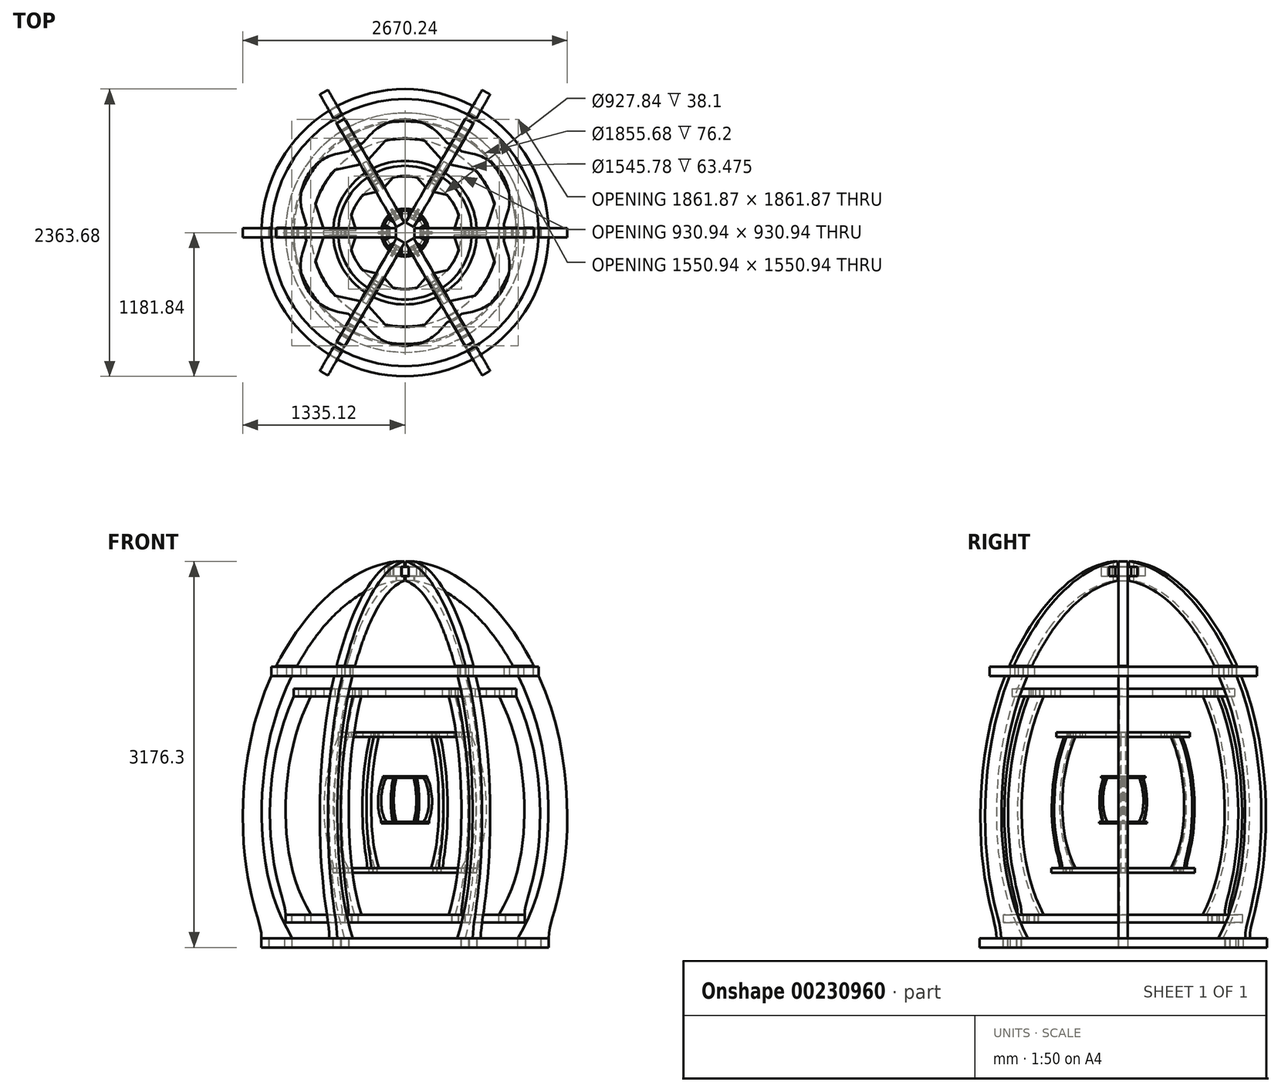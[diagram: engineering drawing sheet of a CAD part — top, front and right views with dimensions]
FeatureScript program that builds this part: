
annotation { "Feature Type Name" : "Feature", "Feature Type Description" : "" }
export const myFeature = defineFeature(function(context is Context, id is Id, definition is map)
    precondition{}
    {
        {
            var Q0;
            Q0=qCreatedBy(makeId("Front.planeOp"),FACE);
            var sketch = newSketch(context, id + "F0", { "sketchPlane" : qUnion([Q0])});
            skLineSegment(sketch, "E0", {"start": v(-1181.84, -1150.9) * mm, "end": v(-927.84, -1150.9) * mm});
            skFitSpline(sketch, "E1", {"points": [v(0, 1953.34) * mm, v(-1100.72, 1005.82) * mm, v(-1321.31, -446.03) * mm, v(-1216.83, -971.67) * mm, v(-1181.84, -1150.9) * mm], "startDerivative": vector(-4000.43, 5.06) * mm, "endDerivative": vector(0, -1489.55) * mm});
            skLineSegment(sketch, "E2", {"start": v(-1099.69, 1008.1) * mm, "end": v(-930.94, 1008.1) * mm});
            skLineSegment(sketch, "E3", {"start": v(-1181.84, -1150.9) * mm, "end": v(-1181.84, -1354.1) * mm});
            skLineSegment(sketch, "E4", {"start": v(-1181.84, -1354.1) * mm, "end": v(-877.04, -1354.1) * mm});
            skLineSegment(sketch, "E5", {"start": v(-877.04, -1354.1) * mm, "end": v(-877.04, -1252.5) * mm});
            skLineSegment(sketch, "E6", {"start": v(-877.04, -1252.5) * mm, "end": v(-927.84, -1252.5) * mm});
            skLineSegment(sketch, "E7", {"start": v(-927.84, -1252.5) * mm, "end": v(-927.84, -1150.9) * mm});
            skFitSpline(sketch, "E8.trimOffspring", {"points": [v(0, -1757.92) * mm, v(-927.84, -1150.9) * mm, v(-1179.31, -127.8) * mm, v(-917.89, 1034.08) * mm, v(0, 1800.66) * mm], "startDerivative": vector(-4973.2, 113.59) * mm, "endDerivative": vector(4756.7, 336.76) * mm});
            skLineSegment(sketch, "E9", {"start": v(-1023.33, 1160.5) * mm, "end": v(-848.12, 1160.5) * mm});
            skLineSegment(sketch, "E10", {"start": v(0, 1953.34) * mm, "end": v(0, 1800.66) * mm});
            skLineSegment(sketch, "E11.bottom", {"start": v(-1118.34, -1074.7) * mm, "end": v(-991.34, -1074.7) * mm});
            skLineSegment(sketch, "E11.top", {"start": v(-1118.34, -1227.1) * mm, "end": v(-991.34, -1227.1) * mm});
            skLineSegment(sketch, "E11.left", {"start": v(-1118.34, -1074.7) * mm, "end": v(-1118.34, -1227.1) * mm});
            skLineSegment(sketch, "E11.right", {"start": v(-991.34, -1074.7) * mm, "end": v(-991.34, -1227.1) * mm});
            skPoint(sketch, "E11.middle", {"position": v(-1054.84, -1150.9) * mm});
            skLineSegment(sketch, "E12.bottom", {"start": v(-1053.41, 1084.3) * mm, "end": v(-977.21, 1084.3) * mm});
            skLineSegment(sketch, "E12.top", {"start": v(-1053.41, 931.9) * mm, "end": v(-977.21, 931.9) * mm});
            skLineSegment(sketch, "E12.left", {"start": v(-1053.41, 1084.3) * mm, "end": v(-1053.41, 931.9) * mm});
            skLineSegment(sketch, "E12.right", {"start": v(-977.21, 1084.3) * mm, "end": v(-977.21, 931.9) * mm});
            skPoint(sketch, "E12.middle", {"position": v(-1015.31, 1008.1) * mm});
            skLineSegment(sketch, "E13", {"start": v(-891.46, 1084.3) * mm, "end": v(-1063.3, 1084.3) * mm});
            skLineSegment(sketch, "E14", {"start": v(-889.38, 1088.12) * mm, "end": v(-1061.37, 1088.12) * mm});
            skLineSegment(sketch, "E15", {"start": v(-76.2, 1949.19) * mm, "end": v(-76.2, 1791.3) * mm});
            skLineSegment(sketch, "E16", {"start": v(-76.2, 1791.3) * mm, "end": v(-76.2, 1829.15) * mm});
            skLineSegment(sketch, "E17", {"start": v(-76.2, 1829.15) * mm, "end": v(-127, 1829.15) * mm});
            skLineSegment(sketch, "E18", {"start": v(-127, 1829.15) * mm, "end": v(-127, 1905.35) * mm});
            skLineSegment(sketch, "E19", {"start": v(-127, 1905.35) * mm, "end": v(-76.2, 1905.35) * mm});
            skLineSegment(sketch, "E20", {"start": v(-889.38, 1088.12) * mm, "end": v(-811.35, 1088.12) * mm});
            skLineSegment(sketch, "E21", {"start": v(-811.35, 1088.12) * mm, "end": v(-680.59, 1399.42) * mm});
            skLineSegment(sketch, "E22", {"start": v(-811.35, 1088.12) * mm, "end": v(-811.35, 1013.84) * mm});
            skLineSegment(sketch, "E23", {"start": v(-811.35, 1013.84) * mm, "end": v(-933.78, 1013.84) * mm});
            skLineSegment(sketch, "E24", {"start": v(-933.78, 1013.84) * mm, "end": v(-933.78, 1088.12) * mm});
            skSolve(sketch);
        }
        {
            var Q0;
            {var subQ5=sQuery(id+"F0.wireOp",EDGE,"E12.bottom");Q0=makeQuery(id+"F0.imprint","IMPRINT",FACE,{"disambiguationData":[TD([[makeQuery(id+"F0.imprint","IMPRINT",EDGE,{"derivedFrom":subQ5}),-1.0]])]});}
            var Q1;
            {var subQ5=sQuery(id+"F0.wireOp",EDGE,"E11.top");Q1=makeQuery(id+"F0.imprint","IMPRINT",FACE,{"disambiguationData":[TD([[makeQuery(id+"F0.imprint","IMPRINT",EDGE,{"derivedFrom":subQ5}),1.0]])]});}
            var Q2;
            {var subQ0=sQuery(id+"F0.wireOp",EDGE,"E11.left");var subQ3=sQuery(id+"F0.wireOp",EDGE,"E0");var subQ4=makeQuery(id+"F0.imprint","INTERSECT",VERTEX,{"derivedFrom":[subQ3,subQ0]});Q2=makeQuery(id+"F0.imprint","IMPRINT",FACE,{"disambiguationData":[TD([[makeQuery(id+"F0.imprint","IMPRINT",EDGE,{"disambiguationData":[TD([[subQ4,-1.0]])],"derivedFrom":subQ3}),1.0]])]});}
            var Q3;
            {var subQ0=sQuery(id+"F0.wireOp",EDGE,"E2");var subQ1=sQuery(id+"F0.wireOp",EDGE,"E1");var subQ2=makeQuery(id+"F0.imprint","INTERSECT",VERTEX,{"derivedFrom":[subQ1,subQ0]});Q3=makeQuery(id+"F0.imprint","IMPRINT",FACE,{"disambiguationData":[TD([[makeQuery(id+"F0.imprint","IMPRINT",EDGE,{"disambiguationData":[TD([[subQ2,-1.0]])],"derivedFrom":subQ0}),-1.0]])]});}
            var Q4;
            {var subQ0=sQuery(id+"F0.wireOp",EDGE,"E8.trimOffspring");var subQ1=sQuery(id+"F0.wireOp",EDGE,"E2");var subQ2=makeQuery(id+"F0.imprint","INTERSECT",VERTEX,{"derivedFrom":[subQ1,subQ0]});Q4=makeQuery(id+"F0.imprint","IMPRINT",FACE,{"disambiguationData":[TD([[makeQuery(id+"F0.imprint","IMPRINT",EDGE,{"disambiguationData":[TD([[subQ2,1.0]])],"derivedFrom":subQ1}),-1.0]])]});}
            var Q5;
            {var subQ0=sQuery(id+"F0.wireOp",EDGE,"E12.left");var subQ5=sQuery(id+"F0.wireOp",EDGE,"E2");var subQ6=makeQuery(id+"F0.imprint","INTERSECT",VERTEX,{"derivedFrom":[subQ5,subQ0]});Q5=makeQuery(id+"F0.imprint","IMPRINT",FACE,{"disambiguationData":[TD([[makeQuery(id+"F0.imprint","IMPRINT",EDGE,{"disambiguationData":[TD([[subQ6,-1.0]])],"derivedFrom":subQ5}),-1.0]])]});}
            var Q6;
            {var subQ0=sQuery(id+"F0.wireOp",EDGE,"E12.left");var subQ1=sQuery(id+"F0.wireOp",EDGE,"E2");var subQ2=makeQuery(id+"F0.imprint","INTERSECT",VERTEX,{"derivedFrom":[subQ1,subQ0]});Q6=makeQuery(id+"F0.imprint","IMPRINT",FACE,{"disambiguationData":[TD([[makeQuery(id+"F0.imprint","IMPRINT",EDGE,{"disambiguationData":[TD([[subQ2,-1.0]])],"derivedFrom":subQ1}),1.0]])]});}
            extrude(context, id + "F1", {"entities" : qUnion([Q0, Q1, Q2, Q3, Q4, Q5, Q6]), "endBound" : BoundingType.SYMMETRIC, "depth" : 76.2 * mm});
        }
        {
            var Q0;
            Q0=makeQuery(id+"F1.opExtrude","SWEPT_BODY",BODY,{"disambiguationData":[OSD([sQuery(id+"F0.wireOp",EDGE,"E0"),sQuery(id+"F0.wireOp",EDGE,"E1"),sQuery(id+"F0.wireOp",EDGE,"E2"),sQuery(id+"F0.wireOp",EDGE,"E8.trimOffspring")])]});
            var Q1;
            Q1=sQuery(id+"F0.wireOp",EDGE,"E10");
            circularPattern(context, id + "F2", {"entities" : qUnion([Q0]), "axis" : qUnion([Q1]), "angle" : 360 * degree, "instanceCount" : 6, "equalSpace" : true});
        }
        {
            var Q0;
            Q0=qCreatedBy(makeId("Top.planeOp"),FACE);
            var Q1;
            Q1=sQuery(id+"F0.wireOp",VERTEX,"E8.trimOffspring.1.internal");
            cPlane(context, id + "F3", {"entities" : qUnion([Q0, Q1]), "cplaneType" : CPlaneType.PLANE_POINT, "offset" : 25.4 * mm, "width" : 152.4 * mm, "height" : 152.4 * mm});
        }
        {
            var Q0;
            Q0=qCreatedBy(id+"F3.planeOp",FACE);
            var sketch = newSketch(context, id + "F4", { "sketchPlane" : qUnion([Q0])});
            skCircle(sketch, "E25", {"center": v(0, 0) * mm, "radius": 1181.84 * mm});
            skCircle(sketch, "E26", {"center": v(0, 0) * mm, "radius": 927.84 * mm});
            skLineSegment(sketch, "E27.bottom", {"start": v(-1118.98, 38.73) * mm, "end": v(-990.7, 38.73) * mm});
            skLineSegment(sketch, "E27.top", {"start": v(-1118.98, -38.74) * mm, "end": v(-990.7, -38.74) * mm});
            skLineSegment(sketch, "E27.left", {"start": v(-1118.98, 38.73) * mm, "end": v(-1118.98, -38.74) * mm});
            skLineSegment(sketch, "E27.right", {"start": v(-990.7, 38.73) * mm, "end": v(-990.7, -38.74) * mm});
            skPoint(sketch, "E27.middle", {"position": v(-1054.84, 0) * mm});
            skLineSegment(sketch, "E28.1.0", {"start": v(-593.03, -949.7) * mm, "end": v(-528.9, -838.6) * mm});
            skLineSegment(sketch, "E28.1.1", {"start": v(-593.03, -949.7) * mm, "end": v(-525.94, -988.43) * mm});
            skLineSegment(sketch, "E28.1.2", {"start": v(-525.94, -988.43) * mm, "end": v(-461.8, -877.34) * mm});
            skLineSegment(sketch, "E28.1.3", {"start": v(-528.9, -838.6) * mm, "end": v(-461.8, -877.34) * mm});
            skLineSegment(sketch, "E28.2.0", {"start": v(525.94, -988.43) * mm, "end": v(461.8, -877.34) * mm});
            skLineSegment(sketch, "E28.2.1", {"start": v(525.94, -988.43) * mm, "end": v(593.03, -949.7) * mm});
            skLineSegment(sketch, "E28.2.2", {"start": v(593.03, -949.7) * mm, "end": v(528.9, -838.6) * mm});
            skLineSegment(sketch, "E28.2.3", {"start": v(461.8, -877.34) * mm, "end": v(528.9, -838.6) * mm});
            skLineSegment(sketch, "E28.3.0", {"start": v(1118.98, -38.74) * mm, "end": v(990.7, -38.74) * mm});
            skLineSegment(sketch, "E28.3.1", {"start": v(1118.98, -38.74) * mm, "end": v(1118.98, 38.73) * mm});
            skLineSegment(sketch, "E28.3.2", {"start": v(1118.98, 38.73) * mm, "end": v(990.7, 38.73) * mm});
            skLineSegment(sketch, "E28.3.3", {"start": v(990.7, -38.74) * mm, "end": v(990.7, 38.73) * mm});
            skLineSegment(sketch, "E28.4.0", {"start": v(593.03, 949.7) * mm, "end": v(528.9, 838.6) * mm});
            skLineSegment(sketch, "E28.4.1", {"start": v(593.03, 949.7) * mm, "end": v(525.94, 988.43) * mm});
            skLineSegment(sketch, "E28.4.2", {"start": v(525.94, 988.43) * mm, "end": v(461.8, 877.34) * mm});
            skLineSegment(sketch, "E28.4.3", {"start": v(528.9, 838.6) * mm, "end": v(461.8, 877.34) * mm});
            skLineSegment(sketch, "E28.5.0", {"start": v(-525.94, 988.43) * mm, "end": v(-461.8, 877.34) * mm});
            skLineSegment(sketch, "E28.5.1", {"start": v(-525.94, 988.43) * mm, "end": v(-593.03, 949.7) * mm});
            skLineSegment(sketch, "E28.5.2", {"start": v(-593.03, 949.7) * mm, "end": v(-528.9, 838.6) * mm});
            skLineSegment(sketch, "E28.5.3", {"start": v(-461.8, 877.34) * mm, "end": v(-528.9, 838.6) * mm});
            skSolve(sketch);
        }
        {
            var Q0;
            Q0=makeQuery(id+"F4.imprint","IMPRINT",FACE,{"disambiguationData":[TD([[makeQuery(id+"F4.imprint","IMPRINT",EDGE,{"derivedFrom":sQuery(id+"F4.wireOp",EDGE,"E25")}),1.0]])]});
            extrude(context, id + "F5", {"entities" : qUnion([Q0]), "oppositeDirection" : true, "depth" : 76.2 * mm});
        }
        {
            var Q0;
            Q0=qCreatedBy(makeId("Top.planeOp"),FACE);
            var Q1;
            Q1=sQuery(id+"F0.wireOp",VERTEX,"E2.end");
            cPlane(context, id + "F6", {"entities" : qUnion([Q0, Q1]), "cplaneType" : CPlaneType.PLANE_POINT, "offset" : 25.4 * mm, "width" : 152.4 * mm, "height" : 152.4 * mm});
        }
        {
            var Q0;
            Q0=qCreatedBy(id+"F6.planeOp",FACE);
            var sketch = newSketch(context, id + "F7", { "sketchPlane" : qUnion([Q0])});
            skCircle(sketch, "E29", {"center": v(0, 0) * mm, "radius": 1099.69 * mm});
            skCircle(sketch, "E30", {"center": v(0, 0) * mm, "radius": 930.94 * mm});
            skLineSegment(sketch, "E31.bottom", {"start": v(-1054.05, 38.74) * mm, "end": v(-976.58, 38.74) * mm});
            skLineSegment(sketch, "E31.top", {"start": v(-1054.05, -38.73) * mm, "end": v(-976.58, -38.73) * mm});
            skLineSegment(sketch, "E31.left", {"start": v(-1054.05, 38.74) * mm, "end": v(-1054.05, -38.73) * mm});
            skLineSegment(sketch, "E31.right", {"start": v(-976.58, 38.74) * mm, "end": v(-976.58, -38.73) * mm});
            skPoint(sketch, "E31.middle", {"position": v(-1015.31, 0) * mm});
            skLineSegment(sketch, "E32.1.0", {"start": v(-560.57, -893.46) * mm, "end": v(-521.83, -826.37) * mm});
            skLineSegment(sketch, "E32.1.1", {"start": v(-560.57, -893.46) * mm, "end": v(-493.48, -932.2) * mm});
            skLineSegment(sketch, "E32.1.2", {"start": v(-493.48, -932.2) * mm, "end": v(-454.74, -865.1) * mm});
            skLineSegment(sketch, "E32.1.3", {"start": v(-521.83, -826.37) * mm, "end": v(-454.74, -865.1) * mm});
            skLineSegment(sketch, "E32.2.0", {"start": v(493.48, -932.2) * mm, "end": v(454.74, -865.1) * mm});
            skLineSegment(sketch, "E32.2.1", {"start": v(493.48, -932.2) * mm, "end": v(560.57, -893.46) * mm});
            skLineSegment(sketch, "E32.2.2", {"start": v(560.57, -893.46) * mm, "end": v(521.83, -826.37) * mm});
            skLineSegment(sketch, "E32.2.3", {"start": v(454.74, -865.1) * mm, "end": v(521.83, -826.37) * mm});
            skLineSegment(sketch, "E32.3.0", {"start": v(1054.05, -38.74) * mm, "end": v(976.58, -38.74) * mm});
            skLineSegment(sketch, "E32.3.1", {"start": v(1054.05, -38.74) * mm, "end": v(1054.05, 38.73) * mm});
            skLineSegment(sketch, "E32.3.2", {"start": v(1054.05, 38.73) * mm, "end": v(976.58, 38.73) * mm});
            skLineSegment(sketch, "E32.3.3", {"start": v(976.58, -38.74) * mm, "end": v(976.58, 38.73) * mm});
            skLineSegment(sketch, "E32.4.0", {"start": v(560.57, 893.46) * mm, "end": v(521.83, 826.37) * mm});
            skLineSegment(sketch, "E32.4.1", {"start": v(560.57, 893.46) * mm, "end": v(493.48, 932.2) * mm});
            skLineSegment(sketch, "E32.4.2", {"start": v(493.48, 932.2) * mm, "end": v(454.74, 865.1) * mm});
            skLineSegment(sketch, "E32.4.3", {"start": v(521.83, 826.37) * mm, "end": v(454.74, 865.1) * mm});
            skLineSegment(sketch, "E32.5.0", {"start": v(-493.48, 932.2) * mm, "end": v(-454.74, 865.1) * mm});
            skLineSegment(sketch, "E32.5.1", {"start": v(-493.48, 932.2) * mm, "end": v(-560.57, 893.46) * mm});
            skLineSegment(sketch, "E32.5.2", {"start": v(-560.57, 893.46) * mm, "end": v(-521.83, 826.37) * mm});
            skLineSegment(sketch, "E32.5.3", {"start": v(-454.74, 865.1) * mm, "end": v(-521.83, 826.37) * mm});
            skLineSegment(sketch, "E33", {"start": v(-930.13, 38.73) * mm, "end": v(-803.13, 38.73) * mm});
            skLineSegment(sketch, "E34", {"start": v(-930.13, -38.74) * mm, "end": v(-803.13, -38.73) * mm});
            skLineSegment(sketch, "E35", {"start": v(-803.13, 38.74) * mm, "end": v(-803.13, -38.74) * mm, "construction": true});
            skLineSegment(sketch, "E36", {"start": v(-803.13, 0) * mm, "end": v(0, 0) * mm, "construction": true});
            skLineSegment(sketch, "E37", {"start": v(-803.13, 38.73) * mm, "end": v(-884.69, 289.77) * mm});
            skLineSegment(sketch, "E38", {"start": v(-803.13, -38.73) * mm, "end": v(-884.69, -289.77) * mm});
            skLineSegment(sketch, "E39.1.0", {"start": v(-435.11, -676.16) * mm, "end": v(-693.3, -621.28) * mm});
            skLineSegment(sketch, "E39.1.1", {"start": v(-498.61, -786.15) * mm, "end": v(-435.11, -676.16) * mm});
            skLineSegment(sketch, "E39.1.2", {"start": v(-431.52, -824.88) * mm, "end": v(-368.02, -714.9) * mm});
            skLineSegment(sketch, "E39.1.3", {"start": v(-368.02, -714.9) * mm, "end": v(-191.4, -911.05) * mm});
            skLineSegment(sketch, "E39.2.0", {"start": v(368.02, -714.9) * mm, "end": v(191.4, -911.05) * mm});
            skLineSegment(sketch, "E39.2.1", {"start": v(431.52, -824.88) * mm, "end": v(368.02, -714.9) * mm});
            skLineSegment(sketch, "E39.2.2", {"start": v(498.61, -786.15) * mm, "end": v(435.11, -676.16) * mm});
            skLineSegment(sketch, "E39.2.3", {"start": v(435.11, -676.16) * mm, "end": v(693.3, -621.28) * mm});
            skLineSegment(sketch, "E39.3.0", {"start": v(803.13, -38.74) * mm, "end": v(884.69, -289.77) * mm});
            skLineSegment(sketch, "E39.3.1", {"start": v(930.13, -38.74) * mm, "end": v(803.13, -38.74) * mm});
            skLineSegment(sketch, "E39.3.2", {"start": v(930.13, 38.73) * mm, "end": v(803.13, 38.73) * mm});
            skLineSegment(sketch, "E39.3.3", {"start": v(803.13, 38.73) * mm, "end": v(884.69, 289.77) * mm});
            skLineSegment(sketch, "E39.4.0", {"start": v(435.11, 676.16) * mm, "end": v(693.3, 621.28) * mm});
            skLineSegment(sketch, "E39.4.1", {"start": v(498.61, 786.15) * mm, "end": v(435.11, 676.16) * mm});
            skLineSegment(sketch, "E39.4.2", {"start": v(431.52, 824.88) * mm, "end": v(368.02, 714.9) * mm});
            skLineSegment(sketch, "E39.4.3", {"start": v(368.02, 714.9) * mm, "end": v(191.4, 911.05) * mm});
            skLineSegment(sketch, "E39.5.0", {"start": v(-368.02, 714.9) * mm, "end": v(-191.4, 911.05) * mm});
            skLineSegment(sketch, "E39.5.1", {"start": v(-431.52, 824.88) * mm, "end": v(-368.02, 714.9) * mm});
            skLineSegment(sketch, "E39.5.2", {"start": v(-498.61, 786.15) * mm, "end": v(-435.11, 676.16) * mm});
            skLineSegment(sketch, "E39.5.3", {"start": v(-435.11, 676.16) * mm, "end": v(-693.3, 621.28) * mm});
            skSolve(sketch);
        }
        {
            var Q0;
            Q0=makeQuery(id+"F7.imprint","IMPRINT",FACE,{"disambiguationData":[TD([[makeQuery(id+"F7.imprint","IMPRINT",EDGE,{"derivedFrom":sQuery(id+"F7.wireOp",EDGE,"E29")}),1.0]])]});
            var Q1;
            {var subQ0=sQuery(id+"F7.wireOp",EDGE,"E34");Q1=makeQuery(id+"F7.imprint","IMPRINT",FACE,{"disambiguationData":[TD([[makeQuery(id+"F7.imprint","IMPRINT",EDGE,{"derivedFrom":subQ0}),-1.0]])]});}
            var Q2;
            {var subQ0=sQuery(id+"F7.wireOp",EDGE,"E33");Q2=makeQuery(id+"F7.imprint","IMPRINT",FACE,{"disambiguationData":[TD([[makeQuery(id+"F7.imprint","IMPRINT",EDGE,{"derivedFrom":subQ0}),1.0]])]});}
            var Q3;
            {var subQ0=sQuery(id+"F7.wireOp",EDGE,"E39.5.2");Q3=makeQuery(id+"F7.imprint","IMPRINT",FACE,{"disambiguationData":[TD([[makeQuery(id+"F7.imprint","IMPRINT",EDGE,{"derivedFrom":subQ0}),-1.0]])]});}
            var Q4;
            {var subQ0=sQuery(id+"F7.wireOp",EDGE,"E39.5.0");Q4=makeQuery(id+"F7.imprint","IMPRINT",FACE,{"disambiguationData":[TD([[makeQuery(id+"F7.imprint","IMPRINT",EDGE,{"derivedFrom":subQ0}),1.0]])]});}
            var Q5;
            {var subQ0=sQuery(id+"F7.wireOp",EDGE,"E39.4.2");Q5=makeQuery(id+"F7.imprint","IMPRINT",FACE,{"disambiguationData":[TD([[makeQuery(id+"F7.imprint","IMPRINT",EDGE,{"derivedFrom":subQ0}),-1.0]])]});}
            var Q6;
            {var subQ0=sQuery(id+"F7.wireOp",EDGE,"E39.4.0");Q6=makeQuery(id+"F7.imprint","IMPRINT",FACE,{"disambiguationData":[TD([[makeQuery(id+"F7.imprint","IMPRINT",EDGE,{"derivedFrom":subQ0}),1.0]])]});}
            var Q7;
            {var subQ0=sQuery(id+"F7.wireOp",EDGE,"E39.3.2");Q7=makeQuery(id+"F7.imprint","IMPRINT",FACE,{"disambiguationData":[TD([[makeQuery(id+"F7.imprint","IMPRINT",EDGE,{"derivedFrom":subQ0}),-1.0]])]});}
            var Q8;
            {var subQ0=sQuery(id+"F7.wireOp",EDGE,"E39.3.0");Q8=makeQuery(id+"F7.imprint","IMPRINT",FACE,{"disambiguationData":[TD([[makeQuery(id+"F7.imprint","IMPRINT",EDGE,{"derivedFrom":subQ0}),1.0]])]});}
            var Q9;
            {var subQ0=sQuery(id+"F7.wireOp",EDGE,"E39.2.2");Q9=makeQuery(id+"F7.imprint","IMPRINT",FACE,{"disambiguationData":[TD([[makeQuery(id+"F7.imprint","IMPRINT",EDGE,{"derivedFrom":subQ0}),-1.0]])]});}
            var Q10;
            {var subQ0=sQuery(id+"F7.wireOp",EDGE,"E39.2.0");Q10=makeQuery(id+"F7.imprint","IMPRINT",FACE,{"disambiguationData":[TD([[makeQuery(id+"F7.imprint","IMPRINT",EDGE,{"derivedFrom":subQ0}),1.0]])]});}
            var Q11;
            {var subQ0=sQuery(id+"F7.wireOp",EDGE,"E39.1.2");Q11=makeQuery(id+"F7.imprint","IMPRINT",FACE,{"disambiguationData":[TD([[makeQuery(id+"F7.imprint","IMPRINT",EDGE,{"derivedFrom":subQ0}),-1.0]])]});}
            var Q12;
            {var subQ0=sQuery(id+"F7.wireOp",EDGE,"E39.1.0");Q12=makeQuery(id+"F7.imprint","IMPRINT",FACE,{"disambiguationData":[TD([[makeQuery(id+"F7.imprint","IMPRINT",EDGE,{"derivedFrom":subQ0}),1.0]])]});}
            extrude(context, id + "F8", {"entities" : qUnion([Q0, Q1, Q2, Q3, Q4, Q5, Q6, Q7, Q8, Q9, Q10, Q11, Q12]), "depth" : 76.2 * mm});
        }
        {
            var Q0;
            Q0=makeQuery(id+"F8.opExtrude","SWEPT_BODY",BODY,{"disambiguationData":[OSD([sQuery(id+"F7.wireOp",EDGE,"E29"),sQuery(id+"F7.wireOp",EDGE,"E30"),sQuery(id+"F7.wireOp",EDGE,"E31.bottom"),sQuery(id+"F7.wireOp",EDGE,"E31.top"),sQuery(id+"F7.wireOp",EDGE,"E31.left"),sQuery(id+"F7.wireOp",EDGE,"E31.right"),sQuery(id+"F7.wireOp",EDGE,"E32.1.0"),sQuery(id+"F7.wireOp",EDGE,"E32.1.1"),sQuery(id+"F7.wireOp",EDGE,"E32.1.2"),sQuery(id+"F7.wireOp",EDGE,"E32.1.3"),sQuery(id+"F7.wireOp",EDGE,"E32.2.0"),sQuery(id+"F7.wireOp",EDGE,"E32.2.1"),sQuery(id+"F7.wireOp",EDGE,"E32.2.2"),sQuery(id+"F7.wireOp",EDGE,"E32.2.3"),sQuery(id+"F7.wireOp",EDGE,"E32.3.0"),sQuery(id+"F7.wireOp",EDGE,"E32.3.1"),sQuery(id+"F7.wireOp",EDGE,"E32.3.2"),sQuery(id+"F7.wireOp",EDGE,"E32.3.3"),sQuery(id+"F7.wireOp",EDGE,"E32.4.0"),sQuery(id+"F7.wireOp",EDGE,"E32.4.1"),sQuery(id+"F7.wireOp",EDGE,"E32.4.2"),sQuery(id+"F7.wireOp",EDGE,"E32.4.3"),sQuery(id+"F7.wireOp",EDGE,"E32.5.0"),sQuery(id+"F7.wireOp",EDGE,"E32.5.1"),sQuery(id+"F7.wireOp",EDGE,"E32.5.2"),sQuery(id+"F7.wireOp",EDGE,"E32.5.3")])]});
            var Q1;
            Q1=makeQuery(id+"F1.opExtrude","SWEPT_BODY",BODY,{"disambiguationData":[OSD([sQuery(id+"F0.wireOp",EDGE,"E0"),sQuery(id+"F0.wireOp",EDGE,"E1"),sQuery(id+"F0.wireOp",EDGE,"E2"),sQuery(id+"F0.wireOp",EDGE,"E8.trimOffspring"),sQuery(id+"F0.wireOp",EDGE,"E11.top"),sQuery(id+"F0.wireOp",EDGE,"E11.left"),sQuery(id+"F0.wireOp",EDGE,"E11.right"),sQuery(id+"F0.wireOp",EDGE,"E12.bottom"),sQuery(id+"F0.wireOp",EDGE,"E12.left"),sQuery(id+"F0.wireOp",EDGE,"E12.right")])]});
            var Q2;
            Q2=makeQuery(id+"F2.opPattern","COPY",BODY,{"derivedFrom":makeQuery(id+"F1.opExtrude","SWEPT_BODY",BODY,{"disambiguationData":[OSD([sQuery(id+"F0.wireOp",EDGE,"E0"),sQuery(id+"F0.wireOp",EDGE,"E1"),sQuery(id+"F0.wireOp",EDGE,"E2"),sQuery(id+"F0.wireOp",EDGE,"E8.trimOffspring"),sQuery(id+"F0.wireOp",EDGE,"E11.top"),sQuery(id+"F0.wireOp",EDGE,"E11.left"),sQuery(id+"F0.wireOp",EDGE,"E11.right"),sQuery(id+"F0.wireOp",EDGE,"E12.bottom"),sQuery(id+"F0.wireOp",EDGE,"E12.left"),sQuery(id+"F0.wireOp",EDGE,"E12.right")])]}),"instanceName":"5"});
            var Q3;
            Q3=makeQuery(id+"F2.opPattern","COPY",BODY,{"derivedFrom":makeQuery(id+"F1.opExtrude","SWEPT_BODY",BODY,{"disambiguationData":[OSD([sQuery(id+"F0.wireOp",EDGE,"E0"),sQuery(id+"F0.wireOp",EDGE,"E1"),sQuery(id+"F0.wireOp",EDGE,"E2"),sQuery(id+"F0.wireOp",EDGE,"E8.trimOffspring"),sQuery(id+"F0.wireOp",EDGE,"E11.top"),sQuery(id+"F0.wireOp",EDGE,"E11.left"),sQuery(id+"F0.wireOp",EDGE,"E11.right"),sQuery(id+"F0.wireOp",EDGE,"E12.bottom"),sQuery(id+"F0.wireOp",EDGE,"E12.left"),sQuery(id+"F0.wireOp",EDGE,"E12.right")])]}),"instanceName":"1"});
            var Q4;
            Q4=makeQuery(id+"F2.opPattern","COPY",BODY,{"derivedFrom":makeQuery(id+"F1.opExtrude","SWEPT_BODY",BODY,{"disambiguationData":[OSD([sQuery(id+"F0.wireOp",EDGE,"E0"),sQuery(id+"F0.wireOp",EDGE,"E1"),sQuery(id+"F0.wireOp",EDGE,"E2"),sQuery(id+"F0.wireOp",EDGE,"E8.trimOffspring"),sQuery(id+"F0.wireOp",EDGE,"E11.top"),sQuery(id+"F0.wireOp",EDGE,"E11.left"),sQuery(id+"F0.wireOp",EDGE,"E11.right"),sQuery(id+"F0.wireOp",EDGE,"E12.bottom"),sQuery(id+"F0.wireOp",EDGE,"E12.left"),sQuery(id+"F0.wireOp",EDGE,"E12.right")])]}),"instanceName":"2"});
            var Q5;
            Q5=makeQuery(id+"F2.opPattern","COPY",BODY,{"derivedFrom":makeQuery(id+"F1.opExtrude","SWEPT_BODY",BODY,{"disambiguationData":[OSD([sQuery(id+"F0.wireOp",EDGE,"E0"),sQuery(id+"F0.wireOp",EDGE,"E1"),sQuery(id+"F0.wireOp",EDGE,"E2"),sQuery(id+"F0.wireOp",EDGE,"E8.trimOffspring"),sQuery(id+"F0.wireOp",EDGE,"E11.top"),sQuery(id+"F0.wireOp",EDGE,"E11.left"),sQuery(id+"F0.wireOp",EDGE,"E11.right"),sQuery(id+"F0.wireOp",EDGE,"E12.bottom"),sQuery(id+"F0.wireOp",EDGE,"E12.left"),sQuery(id+"F0.wireOp",EDGE,"E12.right")])]}),"instanceName":"3"});
            var Q6;
            Q6=makeQuery(id+"F2.opPattern","COPY",BODY,{"derivedFrom":makeQuery(id+"F1.opExtrude","SWEPT_BODY",BODY,{"disambiguationData":[OSD([sQuery(id+"F0.wireOp",EDGE,"E0"),sQuery(id+"F0.wireOp",EDGE,"E1"),sQuery(id+"F0.wireOp",EDGE,"E2"),sQuery(id+"F0.wireOp",EDGE,"E8.trimOffspring"),sQuery(id+"F0.wireOp",EDGE,"E11.top"),sQuery(id+"F0.wireOp",EDGE,"E11.left"),sQuery(id+"F0.wireOp",EDGE,"E11.right"),sQuery(id+"F0.wireOp",EDGE,"E12.bottom"),sQuery(id+"F0.wireOp",EDGE,"E12.left"),sQuery(id+"F0.wireOp",EDGE,"E12.right")])]}),"instanceName":"4"});
            var Q7;
            Q7=makeQuery(id+"F5.opExtrude","SWEPT_BODY",BODY,{"disambiguationData":[OSD([sQuery(id+"F4.wireOp",EDGE,"E25"),sQuery(id+"F4.wireOp",EDGE,"E26"),sQuery(id+"F4.wireOp",EDGE,"E27.bottom"),sQuery(id+"F4.wireOp",EDGE,"E27.top"),sQuery(id+"F4.wireOp",EDGE,"E27.left"),sQuery(id+"F4.wireOp",EDGE,"E27.right"),sQuery(id+"F4.wireOp",EDGE,"E28.1.0"),sQuery(id+"F4.wireOp",EDGE,"E28.1.1"),sQuery(id+"F4.wireOp",EDGE,"E28.1.2"),sQuery(id+"F4.wireOp",EDGE,"E28.1.3"),sQuery(id+"F4.wireOp",EDGE,"E28.2.0"),sQuery(id+"F4.wireOp",EDGE,"E28.2.1"),sQuery(id+"F4.wireOp",EDGE,"E28.2.2"),sQuery(id+"F4.wireOp",EDGE,"E28.2.3"),sQuery(id+"F4.wireOp",EDGE,"E28.3.0"),sQuery(id+"F4.wireOp",EDGE,"E28.3.1"),sQuery(id+"F4.wireOp",EDGE,"E28.3.2"),sQuery(id+"F4.wireOp",EDGE,"E28.3.3"),sQuery(id+"F4.wireOp",EDGE,"E28.4.0"),sQuery(id+"F4.wireOp",EDGE,"E28.4.1"),sQuery(id+"F4.wireOp",EDGE,"E28.4.2"),sQuery(id+"F4.wireOp",EDGE,"E28.4.3"),sQuery(id+"F4.wireOp",EDGE,"E28.5.0"),sQuery(id+"F4.wireOp",EDGE,"E28.5.1"),sQuery(id+"F4.wireOp",EDGE,"E28.5.2"),sQuery(id+"F4.wireOp",EDGE,"E28.5.3")])]});
            var Q8;
            Q8=qCreatedBy(makeId("Origin.pointOp"),VERTEX);
            transform(context, id + "F9", {"entities" : qUnion([Q0, Q1, Q2, Q3, Q4, Q5, Q6, Q7]), "transformType" : TransformType.SCALE_UNIFORMLY, "scale" : .1666, "scalePoint" : qUnion([Q8]), "makeCopy" : true});
        }
        {
            var Q0;
            Q0=makeQuery(id+"F8.opExtrude","SWEPT_BODY",BODY,{"disambiguationData":[OSD([sQuery(id+"F7.wireOp",EDGE,"E29"),sQuery(id+"F7.wireOp",EDGE,"E30"),sQuery(id+"F7.wireOp",EDGE,"E31.bottom"),sQuery(id+"F7.wireOp",EDGE,"E31.top"),sQuery(id+"F7.wireOp",EDGE,"E31.left"),sQuery(id+"F7.wireOp",EDGE,"E31.right"),sQuery(id+"F7.wireOp",EDGE,"E32.1.0"),sQuery(id+"F7.wireOp",EDGE,"E32.1.1"),sQuery(id+"F7.wireOp",EDGE,"E32.1.2"),sQuery(id+"F7.wireOp",EDGE,"E32.1.3"),sQuery(id+"F7.wireOp",EDGE,"E32.2.0"),sQuery(id+"F7.wireOp",EDGE,"E32.2.1"),sQuery(id+"F7.wireOp",EDGE,"E32.2.2"),sQuery(id+"F7.wireOp",EDGE,"E32.2.3"),sQuery(id+"F7.wireOp",EDGE,"E32.3.0"),sQuery(id+"F7.wireOp",EDGE,"E32.3.1"),sQuery(id+"F7.wireOp",EDGE,"E32.3.2"),sQuery(id+"F7.wireOp",EDGE,"E32.3.3"),sQuery(id+"F7.wireOp",EDGE,"E32.4.0"),sQuery(id+"F7.wireOp",EDGE,"E32.4.1"),sQuery(id+"F7.wireOp",EDGE,"E32.4.2"),sQuery(id+"F7.wireOp",EDGE,"E32.4.3"),sQuery(id+"F7.wireOp",EDGE,"E32.5.0"),sQuery(id+"F7.wireOp",EDGE,"E32.5.1"),sQuery(id+"F7.wireOp",EDGE,"E32.5.2"),sQuery(id+"F7.wireOp",EDGE,"E32.5.3")])]});
            var Q1;
            Q1=makeQuery(id+"F1.opExtrude","SWEPT_BODY",BODY,{"disambiguationData":[OSD([sQuery(id+"F0.wireOp",EDGE,"E0"),sQuery(id+"F0.wireOp",EDGE,"E1"),sQuery(id+"F0.wireOp",EDGE,"E2"),sQuery(id+"F0.wireOp",EDGE,"E8.trimOffspring"),sQuery(id+"F0.wireOp",EDGE,"E11.top"),sQuery(id+"F0.wireOp",EDGE,"E11.left"),sQuery(id+"F0.wireOp",EDGE,"E11.right"),sQuery(id+"F0.wireOp",EDGE,"E12.bottom"),sQuery(id+"F0.wireOp",EDGE,"E12.left"),sQuery(id+"F0.wireOp",EDGE,"E12.right")])]});
            var Q2;
            Q2=makeQuery(id+"F2.opPattern","COPY",BODY,{"derivedFrom":makeQuery(id+"F1.opExtrude","SWEPT_BODY",BODY,{"disambiguationData":[OSD([sQuery(id+"F0.wireOp",EDGE,"E0"),sQuery(id+"F0.wireOp",EDGE,"E1"),sQuery(id+"F0.wireOp",EDGE,"E2"),sQuery(id+"F0.wireOp",EDGE,"E8.trimOffspring"),sQuery(id+"F0.wireOp",EDGE,"E11.top"),sQuery(id+"F0.wireOp",EDGE,"E11.left"),sQuery(id+"F0.wireOp",EDGE,"E11.right"),sQuery(id+"F0.wireOp",EDGE,"E12.bottom"),sQuery(id+"F0.wireOp",EDGE,"E12.left"),sQuery(id+"F0.wireOp",EDGE,"E12.right")])]}),"instanceName":"1"});
            var Q3;
            Q3=makeQuery(id+"F2.opPattern","COPY",BODY,{"derivedFrom":makeQuery(id+"F1.opExtrude","SWEPT_BODY",BODY,{"disambiguationData":[OSD([sQuery(id+"F0.wireOp",EDGE,"E0"),sQuery(id+"F0.wireOp",EDGE,"E1"),sQuery(id+"F0.wireOp",EDGE,"E2"),sQuery(id+"F0.wireOp",EDGE,"E8.trimOffspring"),sQuery(id+"F0.wireOp",EDGE,"E11.top"),sQuery(id+"F0.wireOp",EDGE,"E11.left"),sQuery(id+"F0.wireOp",EDGE,"E11.right"),sQuery(id+"F0.wireOp",EDGE,"E12.bottom"),sQuery(id+"F0.wireOp",EDGE,"E12.left"),sQuery(id+"F0.wireOp",EDGE,"E12.right")])]}),"instanceName":"2"});
            var Q4;
            Q4=makeQuery(id+"F2.opPattern","COPY",BODY,{"derivedFrom":makeQuery(id+"F1.opExtrude","SWEPT_BODY",BODY,{"disambiguationData":[OSD([sQuery(id+"F0.wireOp",EDGE,"E0"),sQuery(id+"F0.wireOp",EDGE,"E1"),sQuery(id+"F0.wireOp",EDGE,"E2"),sQuery(id+"F0.wireOp",EDGE,"E8.trimOffspring"),sQuery(id+"F0.wireOp",EDGE,"E11.top"),sQuery(id+"F0.wireOp",EDGE,"E11.left"),sQuery(id+"F0.wireOp",EDGE,"E11.right"),sQuery(id+"F0.wireOp",EDGE,"E12.bottom"),sQuery(id+"F0.wireOp",EDGE,"E12.left"),sQuery(id+"F0.wireOp",EDGE,"E12.right")])]}),"instanceName":"3"});
            var Q5;
            Q5=makeQuery(id+"F2.opPattern","COPY",BODY,{"derivedFrom":makeQuery(id+"F1.opExtrude","SWEPT_BODY",BODY,{"disambiguationData":[OSD([sQuery(id+"F0.wireOp",EDGE,"E0"),sQuery(id+"F0.wireOp",EDGE,"E1"),sQuery(id+"F0.wireOp",EDGE,"E2"),sQuery(id+"F0.wireOp",EDGE,"E8.trimOffspring"),sQuery(id+"F0.wireOp",EDGE,"E11.top"),sQuery(id+"F0.wireOp",EDGE,"E11.left"),sQuery(id+"F0.wireOp",EDGE,"E11.right"),sQuery(id+"F0.wireOp",EDGE,"E12.bottom"),sQuery(id+"F0.wireOp",EDGE,"E12.left"),sQuery(id+"F0.wireOp",EDGE,"E12.right")])]}),"instanceName":"4"});
            var Q6;
            Q6=makeQuery(id+"F5.opExtrude","SWEPT_BODY",BODY,{"disambiguationData":[OSD([sQuery(id+"F4.wireOp",EDGE,"E25"),sQuery(id+"F4.wireOp",EDGE,"E26"),sQuery(id+"F4.wireOp",EDGE,"E27.bottom"),sQuery(id+"F4.wireOp",EDGE,"E27.top"),sQuery(id+"F4.wireOp",EDGE,"E27.left"),sQuery(id+"F4.wireOp",EDGE,"E27.right"),sQuery(id+"F4.wireOp",EDGE,"E28.1.0"),sQuery(id+"F4.wireOp",EDGE,"E28.1.1"),sQuery(id+"F4.wireOp",EDGE,"E28.1.2"),sQuery(id+"F4.wireOp",EDGE,"E28.1.3"),sQuery(id+"F4.wireOp",EDGE,"E28.2.0"),sQuery(id+"F4.wireOp",EDGE,"E28.2.1"),sQuery(id+"F4.wireOp",EDGE,"E28.2.2"),sQuery(id+"F4.wireOp",EDGE,"E28.2.3"),sQuery(id+"F4.wireOp",EDGE,"E28.3.0"),sQuery(id+"F4.wireOp",EDGE,"E28.3.1"),sQuery(id+"F4.wireOp",EDGE,"E28.3.2"),sQuery(id+"F4.wireOp",EDGE,"E28.3.3"),sQuery(id+"F4.wireOp",EDGE,"E28.4.0"),sQuery(id+"F4.wireOp",EDGE,"E28.4.1"),sQuery(id+"F4.wireOp",EDGE,"E28.4.2"),sQuery(id+"F4.wireOp",EDGE,"E28.4.3"),sQuery(id+"F4.wireOp",EDGE,"E28.5.0"),sQuery(id+"F4.wireOp",EDGE,"E28.5.1"),sQuery(id+"F4.wireOp",EDGE,"E28.5.2"),sQuery(id+"F4.wireOp",EDGE,"E28.5.3")])]});
            var Q7;
            Q7=makeQuery(id+"F2.opPattern","COPY",BODY,{"derivedFrom":makeQuery(id+"F1.opExtrude","SWEPT_BODY",BODY,{"disambiguationData":[OSD([sQuery(id+"F0.wireOp",EDGE,"E0"),sQuery(id+"F0.wireOp",EDGE,"E1"),sQuery(id+"F0.wireOp",EDGE,"E2"),sQuery(id+"F0.wireOp",EDGE,"E8.trimOffspring"),sQuery(id+"F0.wireOp",EDGE,"E11.top"),sQuery(id+"F0.wireOp",EDGE,"E11.left"),sQuery(id+"F0.wireOp",EDGE,"E11.right"),sQuery(id+"F0.wireOp",EDGE,"E12.bottom"),sQuery(id+"F0.wireOp",EDGE,"E12.left"),sQuery(id+"F0.wireOp",EDGE,"E12.right")])]}),"instanceName":"5"});
            var Q8;
            Q8=qCreatedBy(makeId("Origin.pointOp"),VERTEX);
            transform(context, id + "F10", {"entities" : qUnion([Q0, Q1, Q2, Q3, Q4, Q5, Q6, Q7]), "transformType" : TransformType.SCALE_UNIFORMLY, "scale" : .833, "scalePoint" : qUnion([Q8]), "makeCopy" : true});
        }
        {
            var Q0;
            Q0=makeQuery(id+"F8.opExtrude","SWEPT_BODY",BODY,{"disambiguationData":[OSD([sQuery(id+"F7.wireOp",EDGE,"E29"),sQuery(id+"F7.wireOp",EDGE,"E30"),sQuery(id+"F7.wireOp",EDGE,"E31.bottom"),sQuery(id+"F7.wireOp",EDGE,"E31.top"),sQuery(id+"F7.wireOp",EDGE,"E31.left"),sQuery(id+"F7.wireOp",EDGE,"E31.right"),sQuery(id+"F7.wireOp",EDGE,"E32.1.0"),sQuery(id+"F7.wireOp",EDGE,"E32.1.1"),sQuery(id+"F7.wireOp",EDGE,"E32.1.2"),sQuery(id+"F7.wireOp",EDGE,"E32.1.3"),sQuery(id+"F7.wireOp",EDGE,"E32.2.0"),sQuery(id+"F7.wireOp",EDGE,"E32.2.1"),sQuery(id+"F7.wireOp",EDGE,"E32.2.2"),sQuery(id+"F7.wireOp",EDGE,"E32.2.3"),sQuery(id+"F7.wireOp",EDGE,"E32.3.0"),sQuery(id+"F7.wireOp",EDGE,"E32.3.1"),sQuery(id+"F7.wireOp",EDGE,"E32.3.2"),sQuery(id+"F7.wireOp",EDGE,"E32.3.3"),sQuery(id+"F7.wireOp",EDGE,"E32.4.0"),sQuery(id+"F7.wireOp",EDGE,"E32.4.1"),sQuery(id+"F7.wireOp",EDGE,"E32.4.2"),sQuery(id+"F7.wireOp",EDGE,"E32.4.3"),sQuery(id+"F7.wireOp",EDGE,"E32.5.0"),sQuery(id+"F7.wireOp",EDGE,"E32.5.1"),sQuery(id+"F7.wireOp",EDGE,"E32.5.2"),sQuery(id+"F7.wireOp",EDGE,"E32.5.3")])]});
            var Q1;
            Q1=makeQuery(id+"F2.opPattern","COPY",BODY,{"derivedFrom":makeQuery(id+"F1.opExtrude","SWEPT_BODY",BODY,{"disambiguationData":[OSD([sQuery(id+"F0.wireOp",EDGE,"E0"),sQuery(id+"F0.wireOp",EDGE,"E1"),sQuery(id+"F0.wireOp",EDGE,"E2"),sQuery(id+"F0.wireOp",EDGE,"E8.trimOffspring"),sQuery(id+"F0.wireOp",EDGE,"E11.top"),sQuery(id+"F0.wireOp",EDGE,"E11.left"),sQuery(id+"F0.wireOp",EDGE,"E11.right"),sQuery(id+"F0.wireOp",EDGE,"E12.bottom"),sQuery(id+"F0.wireOp",EDGE,"E12.left"),sQuery(id+"F0.wireOp",EDGE,"E12.right")])]}),"instanceName":"5"});
            var Q2;
            Q2=makeQuery(id+"F1.opExtrude","SWEPT_BODY",BODY,{"disambiguationData":[OSD([sQuery(id+"F0.wireOp",EDGE,"E0"),sQuery(id+"F0.wireOp",EDGE,"E1"),sQuery(id+"F0.wireOp",EDGE,"E2"),sQuery(id+"F0.wireOp",EDGE,"E8.trimOffspring"),sQuery(id+"F0.wireOp",EDGE,"E11.top"),sQuery(id+"F0.wireOp",EDGE,"E11.left"),sQuery(id+"F0.wireOp",EDGE,"E11.right"),sQuery(id+"F0.wireOp",EDGE,"E12.bottom"),sQuery(id+"F0.wireOp",EDGE,"E12.left"),sQuery(id+"F0.wireOp",EDGE,"E12.right")])]});
            var Q3;
            Q3=makeQuery(id+"F2.opPattern","COPY",BODY,{"derivedFrom":makeQuery(id+"F1.opExtrude","SWEPT_BODY",BODY,{"disambiguationData":[OSD([sQuery(id+"F0.wireOp",EDGE,"E0"),sQuery(id+"F0.wireOp",EDGE,"E1"),sQuery(id+"F0.wireOp",EDGE,"E2"),sQuery(id+"F0.wireOp",EDGE,"E8.trimOffspring"),sQuery(id+"F0.wireOp",EDGE,"E11.top"),sQuery(id+"F0.wireOp",EDGE,"E11.left"),sQuery(id+"F0.wireOp",EDGE,"E11.right"),sQuery(id+"F0.wireOp",EDGE,"E12.bottom"),sQuery(id+"F0.wireOp",EDGE,"E12.left"),sQuery(id+"F0.wireOp",EDGE,"E12.right")])]}),"instanceName":"4"});
            var Q4;
            Q4=makeQuery(id+"F2.opPattern","COPY",BODY,{"derivedFrom":makeQuery(id+"F1.opExtrude","SWEPT_BODY",BODY,{"disambiguationData":[OSD([sQuery(id+"F0.wireOp",EDGE,"E0"),sQuery(id+"F0.wireOp",EDGE,"E1"),sQuery(id+"F0.wireOp",EDGE,"E2"),sQuery(id+"F0.wireOp",EDGE,"E8.trimOffspring"),sQuery(id+"F0.wireOp",EDGE,"E11.top"),sQuery(id+"F0.wireOp",EDGE,"E11.left"),sQuery(id+"F0.wireOp",EDGE,"E11.right"),sQuery(id+"F0.wireOp",EDGE,"E12.bottom"),sQuery(id+"F0.wireOp",EDGE,"E12.left"),sQuery(id+"F0.wireOp",EDGE,"E12.right")])]}),"instanceName":"3"});
            var Q5;
            Q5=makeQuery(id+"F2.opPattern","COPY",BODY,{"derivedFrom":makeQuery(id+"F1.opExtrude","SWEPT_BODY",BODY,{"disambiguationData":[OSD([sQuery(id+"F0.wireOp",EDGE,"E0"),sQuery(id+"F0.wireOp",EDGE,"E1"),sQuery(id+"F0.wireOp",EDGE,"E2"),sQuery(id+"F0.wireOp",EDGE,"E8.trimOffspring"),sQuery(id+"F0.wireOp",EDGE,"E11.top"),sQuery(id+"F0.wireOp",EDGE,"E11.left"),sQuery(id+"F0.wireOp",EDGE,"E11.right"),sQuery(id+"F0.wireOp",EDGE,"E12.bottom"),sQuery(id+"F0.wireOp",EDGE,"E12.left"),sQuery(id+"F0.wireOp",EDGE,"E12.right")])]}),"instanceName":"1"});
            var Q6;
            Q6=makeQuery(id+"F2.opPattern","COPY",BODY,{"derivedFrom":makeQuery(id+"F1.opExtrude","SWEPT_BODY",BODY,{"disambiguationData":[OSD([sQuery(id+"F0.wireOp",EDGE,"E0"),sQuery(id+"F0.wireOp",EDGE,"E1"),sQuery(id+"F0.wireOp",EDGE,"E2"),sQuery(id+"F0.wireOp",EDGE,"E8.trimOffspring"),sQuery(id+"F0.wireOp",EDGE,"E11.top"),sQuery(id+"F0.wireOp",EDGE,"E11.left"),sQuery(id+"F0.wireOp",EDGE,"E11.right"),sQuery(id+"F0.wireOp",EDGE,"E12.bottom"),sQuery(id+"F0.wireOp",EDGE,"E12.left"),sQuery(id+"F0.wireOp",EDGE,"E12.right")])]}),"instanceName":"2"});
            var Q7;
            Q7=makeQuery(id+"F5.opExtrude","SWEPT_BODY",BODY,{"disambiguationData":[OSD([sQuery(id+"F4.wireOp",EDGE,"E25"),sQuery(id+"F4.wireOp",EDGE,"E26"),sQuery(id+"F4.wireOp",EDGE,"E27.bottom"),sQuery(id+"F4.wireOp",EDGE,"E27.top"),sQuery(id+"F4.wireOp",EDGE,"E27.left"),sQuery(id+"F4.wireOp",EDGE,"E27.right"),sQuery(id+"F4.wireOp",EDGE,"E28.1.0"),sQuery(id+"F4.wireOp",EDGE,"E28.1.1"),sQuery(id+"F4.wireOp",EDGE,"E28.1.2"),sQuery(id+"F4.wireOp",EDGE,"E28.1.3"),sQuery(id+"F4.wireOp",EDGE,"E28.2.0"),sQuery(id+"F4.wireOp",EDGE,"E28.2.1"),sQuery(id+"F4.wireOp",EDGE,"E28.2.2"),sQuery(id+"F4.wireOp",EDGE,"E28.2.3"),sQuery(id+"F4.wireOp",EDGE,"E28.3.0"),sQuery(id+"F4.wireOp",EDGE,"E28.3.1"),sQuery(id+"F4.wireOp",EDGE,"E28.3.2"),sQuery(id+"F4.wireOp",EDGE,"E28.3.3"),sQuery(id+"F4.wireOp",EDGE,"E28.4.0"),sQuery(id+"F4.wireOp",EDGE,"E28.4.1"),sQuery(id+"F4.wireOp",EDGE,"E28.4.2"),sQuery(id+"F4.wireOp",EDGE,"E28.4.3"),sQuery(id+"F4.wireOp",EDGE,"E28.5.0"),sQuery(id+"F4.wireOp",EDGE,"E28.5.1"),sQuery(id+"F4.wireOp",EDGE,"E28.5.2"),sQuery(id+"F4.wireOp",EDGE,"E28.5.3")])]});
            var Q8;
            Q8=qCreatedBy(makeId("Origin.pointOp"),VERTEX);
            transform(context, id + "F11", {"entities" : qUnion([Q0, Q1, Q2, Q3, Q4, Q5, Q6, Q7]), "transformType" : TransformType.SCALE_UNIFORMLY, "scale" : .5, "scalePoint" : qUnion([Q8]), "makeCopy" : true});
        }
        {
            var Q0;
            {var subQ4=sQuery(id+"F0.wireOp",EDGE,"E9");Q0=makeQuery(id+"F0.imprint","IMPRINT",FACE,{"disambiguationData":[TD([[makeQuery(id+"F0.imprint","IMPRINT",EDGE,{"derivedFrom":subQ4}),-1.0]])]});}
            var Q1;
            {var subQ2=sQuery(id+"F0.wireOp",EDGE,"E9");Q1=makeQuery(id+"F0.imprint","IMPRINT",FACE,{"disambiguationData":[TD([[makeQuery(id+"F0.imprint","IMPRINT",EDGE,{"derivedFrom":subQ2}),1.0]])]});}
            extrude(context, id + "F12", {"entities" : qUnion([Q0, Q1]), "operationType" : NewBodyOperationType.ADD, "endBound" : BoundingType.SYMMETRIC, "depth" : 76.2 * mm});
        }
        {
            var Q0;
            Q0=makeQuery(id+"F12.opExtrude","SWEPT_BODY",BODY,{"disambiguationData":[OSD([sQuery(id+"F0.wireOp",EDGE,"E1"),sQuery(id+"F0.wireOp",EDGE,"E8.trimOffspring"),sQuery(id+"F0.wireOp",EDGE,"E10"),sQuery(id+"F0.wireOp",EDGE,"E14")])]});
            var Q1;
            Q1=sQuery(id+"F0.wireOp",EDGE,"E10");
            circularPattern(context, id + "F13", {"entities" : qUnion([Q0]), "axis" : qUnion([Q1]), "angle" : 360 * degree, "instanceCount" : 6, "equalSpace" : true});
        }
        {
            var Q0;
            Q0=makeQuery(id+"F13.opPattern","COPY",FACE,{"derivedFrom":makeQuery(id+"F12.opExtrude","SWEPT_FACE",FACE,{"disambiguationData":[OSD([sQuery(id+"F0.wireOp",EDGE,"E17")])]}),"instanceName":"5"});
            var sketch = newSketch(context, id + "F14", { "sketchPlane" : qUnion([Q0])});
            skCircle(sketch, "E40", {"center": v(0, 0) * mm, "radius": 127 * mm});
            skLineSegment(sketch, "E41", {"start": v(-121.45, 37.13) * mm, "end": v(-170.95, 65.7) * mm});
            skLineSegment(sketch, "E42", {"start": v(-170.95, 65.7) * mm, "end": v(-142.37, 115.2) * mm});
            skLineSegment(sketch, "E43", {"start": v(-142.37, 115.2) * mm, "end": v(-92.88, 86.62) * mm});
            skLineSegment(sketch, "E44", {"start": v(-156.66, 90.45) * mm, "end": v(0, 0) * mm});
            skLineSegment(sketch, "E45", {"start": v(0, 0) * mm, "end": v(-54.91, 0) * mm, "construction": true});
            skLineSegment(sketch, "E46.1.0", {"start": v(-170.95, -65.7) * mm, "end": v(-121.45, -37.13) * mm});
            skLineSegment(sketch, "E46.1.1", {"start": v(-142.37, -115.2) * mm, "end": v(-170.95, -65.7) * mm});
            skLineSegment(sketch, "E46.1.2", {"start": v(-92.88, -86.62) * mm, "end": v(-142.37, -115.2) * mm});
            skLineSegment(sketch, "E46.2.0", {"start": v(-28.57, -180.9) * mm, "end": v(-28.57, -123.74) * mm});
            skLineSegment(sketch, "E46.2.1", {"start": v(28.58, -180.9) * mm, "end": v(-28.57, -180.9) * mm});
            skLineSegment(sketch, "E46.2.2", {"start": v(28.58, -123.74) * mm, "end": v(28.58, -180.9) * mm});
            skLineSegment(sketch, "E46.3.0", {"start": v(142.37, -115.2) * mm, "end": v(92.88, -86.62) * mm});
            skLineSegment(sketch, "E46.3.1", {"start": v(170.95, -65.7) * mm, "end": v(142.37, -115.2) * mm});
            skLineSegment(sketch, "E46.3.2", {"start": v(121.45, -37.13) * mm, "end": v(170.95, -65.7) * mm});
            skLineSegment(sketch, "E46.4.0", {"start": v(170.95, 65.7) * mm, "end": v(121.45, 37.13) * mm});
            skLineSegment(sketch, "E46.4.1", {"start": v(142.37, 115.2) * mm, "end": v(170.95, 65.7) * mm});
            skLineSegment(sketch, "E46.4.2", {"start": v(92.88, 86.62) * mm, "end": v(142.37, 115.2) * mm});
            skLineSegment(sketch, "E46.5.0", {"start": v(28.57, 180.9) * mm, "end": v(28.57, 123.74) * mm});
            skLineSegment(sketch, "E46.5.1", {"start": v(-28.58, 180.9) * mm, "end": v(28.57, 180.9) * mm});
            skLineSegment(sketch, "E46.5.2", {"start": v(-28.58, 123.74) * mm, "end": v(-28.58, 180.9) * mm});
            skSolve(sketch);
        }
        {
            var Q0;
            Q0=qSketchRegion(id+"F14",true);
            extrude(context, id + "F15", {"entities" : qUnion([Q0]), "depth" : 76.2 * mm});
        }
        {
            var Q0;
            Q0=makeQuery(id+"F8.opExtrude","SWEPT_EDGE",EDGE,{"disambiguationData":[OSD([sQuery(id+"F7.wireOp",EDGE,"E30"),sQuery(id+"F7.wireOp",EDGE,"E38")])]});
            var Q1;
            Q1=makeQuery(id+"F8.opExtrude","SWEPT_EDGE",EDGE,{"disambiguationData":[OSD([sQuery(id+"F7.wireOp",EDGE,"E30"),sQuery(id+"F7.wireOp",EDGE,"E37")])]});
            var Q2;
            Q2=makeQuery(id+"F8.opExtrude","SWEPT_EDGE",EDGE,{"disambiguationData":[OSD([sQuery(id+"F7.wireOp",EDGE,"E30"),sQuery(id+"F7.wireOp",EDGE,"E39.5.3")])]});
            var Q3;
            Q3=makeQuery(id+"F8.opExtrude","SWEPT_EDGE",EDGE,{"disambiguationData":[OSD([sQuery(id+"F7.wireOp",EDGE,"E30"),sQuery(id+"F7.wireOp",EDGE,"E39.5.0")])]});
            var Q4;
            Q4=makeQuery(id+"F8.opExtrude","SWEPT_EDGE",EDGE,{"disambiguationData":[OSD([sQuery(id+"F7.wireOp",EDGE,"E30"),sQuery(id+"F7.wireOp",EDGE,"E39.4.3")])]});
            var Q5;
            Q5=makeQuery(id+"F8.opExtrude","SWEPT_EDGE",EDGE,{"disambiguationData":[OSD([sQuery(id+"F7.wireOp",EDGE,"E30"),sQuery(id+"F7.wireOp",EDGE,"E39.4.0")])]});
            var Q6;
            Q6=makeQuery(id+"F8.opExtrude","SWEPT_EDGE",EDGE,{"disambiguationData":[OSD([sQuery(id+"F7.wireOp",EDGE,"E30"),sQuery(id+"F7.wireOp",EDGE,"E39.3.3")])]});
            var Q7;
            Q7=makeQuery(id+"F8.opExtrude","SWEPT_EDGE",EDGE,{"disambiguationData":[OSD([sQuery(id+"F7.wireOp",EDGE,"E30"),sQuery(id+"F7.wireOp",EDGE,"E39.3.0")])]});
            var Q8;
            Q8=makeQuery(id+"F8.opExtrude","SWEPT_EDGE",EDGE,{"disambiguationData":[OSD([sQuery(id+"F7.wireOp",EDGE,"E30"),sQuery(id+"F7.wireOp",EDGE,"E39.2.3")])]});
            var Q9;
            Q9=makeQuery(id+"F8.opExtrude","SWEPT_EDGE",EDGE,{"disambiguationData":[OSD([sQuery(id+"F7.wireOp",EDGE,"E30"),sQuery(id+"F7.wireOp",EDGE,"E39.2.0")])]});
            var Q10;
            Q10=makeQuery(id+"F8.opExtrude","SWEPT_EDGE",EDGE,{"disambiguationData":[OSD([sQuery(id+"F7.wireOp",EDGE,"E30"),sQuery(id+"F7.wireOp",EDGE,"E39.1.3")])]});
            var Q11;
            Q11=makeQuery(id+"F8.opExtrude","SWEPT_EDGE",EDGE,{"disambiguationData":[OSD([sQuery(id+"F7.wireOp",EDGE,"E30"),sQuery(id+"F7.wireOp",EDGE,"E39.1.0")])]});
            fillet(context, id + "F16", {"entities" : qUnion([Q0, Q1, Q2, Q3, Q4, Q5, Q6, Q7, Q8, Q9, Q10, Q11]), "radius" : 381 * mm, "tangentPropagation" : true, "allowEdgeOverflow" : false});
        }
        {
            var Q0;
            Q0=makeQuery(id+"F8.opExtrude","SWEPT_EDGE",EDGE,{"disambiguationData":[OSD([sQuery(id+"F7.wireOp",EDGE,"E39.4.0"),sQuery(id+"F7.wireOp",EDGE,"E39.4.1")])]});
            var Q1;
            Q1=makeQuery(id+"F8.opExtrude","SWEPT_EDGE",EDGE,{"disambiguationData":[OSD([sQuery(id+"F7.wireOp",EDGE,"E39.4.2"),sQuery(id+"F7.wireOp",EDGE,"E39.4.3")])]});
            var Q2;
            Q2=makeQuery(id+"F8.opExtrude","SWEPT_EDGE",EDGE,{"disambiguationData":[OSD([sQuery(id+"F7.wireOp",EDGE,"E39.5.0"),sQuery(id+"F7.wireOp",EDGE,"E39.5.1")])]});
            var Q3;
            Q3=makeQuery(id+"F8.opExtrude","SWEPT_EDGE",EDGE,{"disambiguationData":[OSD([sQuery(id+"F7.wireOp",EDGE,"E39.5.2"),sQuery(id+"F7.wireOp",EDGE,"E39.5.3")])]});
            var Q4;
            Q4=makeQuery(id+"F8.opExtrude","SWEPT_EDGE",EDGE,{"disambiguationData":[OSD([sQuery(id+"F7.wireOp",EDGE,"E33"),sQuery(id+"F7.wireOp",EDGE,"E37")])]});
            var Q5;
            Q5=makeQuery(id+"F8.opExtrude","SWEPT_EDGE",EDGE,{"disambiguationData":[OSD([sQuery(id+"F7.wireOp",EDGE,"E34"),sQuery(id+"F7.wireOp",EDGE,"E38")])]});
            var Q6;
            Q6=makeQuery(id+"F8.opExtrude","SWEPT_EDGE",EDGE,{"disambiguationData":[OSD([sQuery(id+"F7.wireOp",EDGE,"E39.1.0"),sQuery(id+"F7.wireOp",EDGE,"E39.1.1")])]});
            var Q7;
            Q7=makeQuery(id+"F8.opExtrude","SWEPT_EDGE",EDGE,{"disambiguationData":[OSD([sQuery(id+"F7.wireOp",EDGE,"E39.1.2"),sQuery(id+"F7.wireOp",EDGE,"E39.1.3")])]});
            var Q8;
            Q8=makeQuery(id+"F8.opExtrude","SWEPT_EDGE",EDGE,{"disambiguationData":[OSD([sQuery(id+"F7.wireOp",EDGE,"E39.2.0"),sQuery(id+"F7.wireOp",EDGE,"E39.2.1")])]});
            var Q9;
            Q9=makeQuery(id+"F8.opExtrude","SWEPT_EDGE",EDGE,{"disambiguationData":[OSD([sQuery(id+"F7.wireOp",EDGE,"E39.2.2"),sQuery(id+"F7.wireOp",EDGE,"E39.2.3")])]});
            var Q10;
            Q10=makeQuery(id+"F8.opExtrude","SWEPT_EDGE",EDGE,{"disambiguationData":[OSD([sQuery(id+"F7.wireOp",EDGE,"E39.3.0"),sQuery(id+"F7.wireOp",EDGE,"E39.3.1")])]});
            var Q11;
            Q11=makeQuery(id+"F8.opExtrude","SWEPT_EDGE",EDGE,{"disambiguationData":[OSD([sQuery(id+"F7.wireOp",EDGE,"E39.3.2"),sQuery(id+"F7.wireOp",EDGE,"E39.3.3")])]});
            fillet(context, id + "F17", {"entities" : qUnion([Q0, Q1, Q2, Q3, Q4, Q5, Q6, Q7, Q8, Q9, Q10, Q11]), "radius" : 25.4 * mm, "tangentPropagation" : true, "allowEdgeOverflow" : false});
        }
    });
